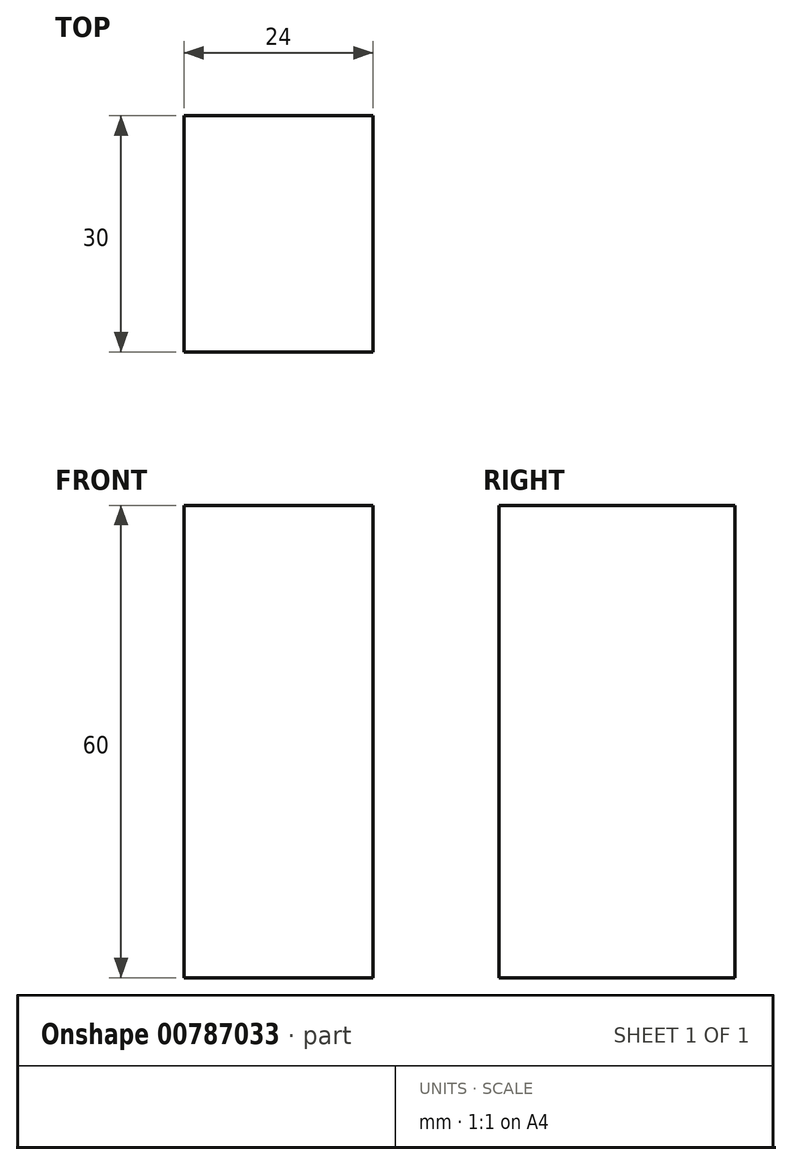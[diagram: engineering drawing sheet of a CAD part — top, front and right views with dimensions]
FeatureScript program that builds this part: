
annotation { "Feature Type Name" : "Feature", "Feature Type Description" : "" }
export const myFeature = defineFeature(function(context is Context, id is Id, definition is map)
    precondition{}
    {
        {
            var Q0;
            Q0=qCreatedBy(makeId("Top.planeOp"),FACE);
            var sketch = newSketch(context, id + "F0", { "sketchPlane" : qUnion([Q0])});
            skLineSegment(sketch, "E0.bottom", {"start": v(-30.54, 4.56) * mm, "end": v(-6.54, 4.56) * mm});
            skLineSegment(sketch, "E0.top", {"start": v(-30.54, -25.44) * mm, "end": v(-6.54, -25.44) * mm});
            skLineSegment(sketch, "E0.left", {"start": v(-30.54, 4.56) * mm, "end": v(-30.54, -25.44) * mm});
            skLineSegment(sketch, "E0.right", {"start": v(-6.54, 4.56) * mm, "end": v(-6.54, -25.44) * mm});
            skSolve(sketch);
        }
        {
            var Q0;
            Q0=makeQuery(id+"F0.imprint","IMPRINT",FACE,{"disambiguationData":[TD([[makeQuery(id+"F0.imprint","IMPRINT",EDGE,{"derivedFrom":sQuery(id+"F0.wireOp",EDGE,"E0.bottom")}),-1.0]])]});
            extrude(context, id + "F1", {"entities" : qUnion([Q0]), "depth" : 60 * mm, "offsetDistance" : 25 * mm});
        }
    });
